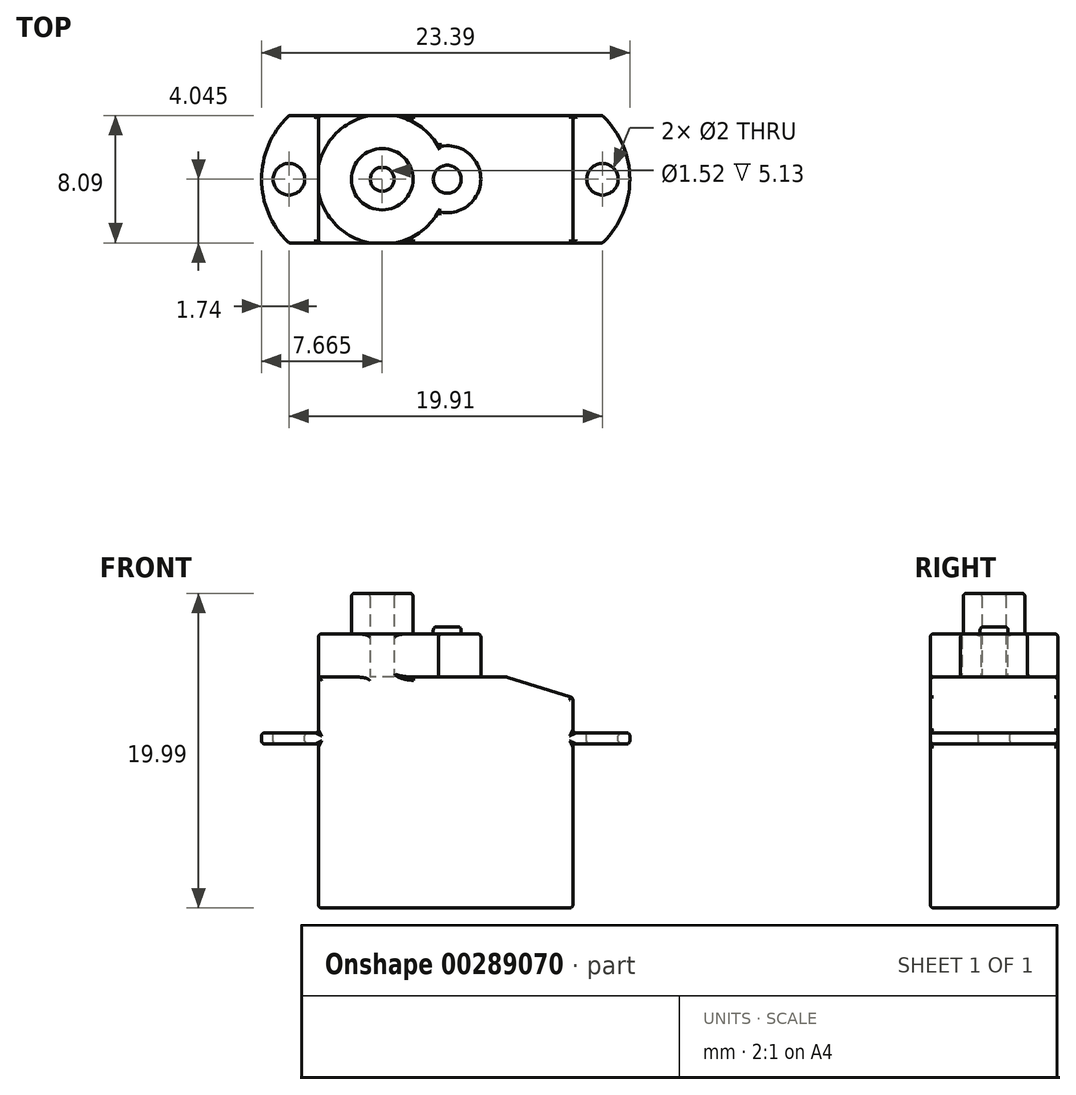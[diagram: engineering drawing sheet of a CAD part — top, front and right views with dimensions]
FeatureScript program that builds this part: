
annotation { "Feature Type Name" : "Feature", "Feature Type Description" : "" }
export const myFeature = defineFeature(function(context is Context, id is Id, definition is map)
    precondition{}
    {
        {
            var Q0;
            Q0=qCreatedBy(makeId("Top.planeOp"),FACE);
            var sketch = newSketch(context, id + "F0", { "sketchPlane" : qUnion([Q0])});
            skLineSegment(sketch, "E0.bottom", {"start": v(0, 0) * mm, "end": v(16.15, 0) * mm});
            skLineSegment(sketch, "E0.top", {"start": v(0, -8.1) * mm, "end": v(16.15, -8.1) * mm});
            skLineSegment(sketch, "E0.left", {"start": v(0, 0) * mm, "end": v(0, -8.1) * mm});
            skLineSegment(sketch, "E0.right", {"start": v(16.15, 0) * mm, "end": v(16.15, -8.1) * mm});
            skLineSegment(sketch, "E1", {"start": v(0, -4.05) * mm, "end": v(4.05, -4.05) * mm});
            skCircle(sketch, "E2", {"center": v(4.05, -4.05) * mm, "radius": 4.13 * mm});
            skCircle(sketch, "E3", {"center": v(8.18, -4.05) * mm, "radius": 2.13 * mm});
            skCircle(sketch, "E4", {"center": v(4.05, -4.05) * mm, "radius": 1.95 * mm});
            skCircle(sketch, "E5", {"center": v(8.18, -4.05) * mm, "radius": 0.9 * mm});
            skLineSegment(sketch, "E6", {"start": v(0, 0) * mm, "end": v(-1.88, 0) * mm});
            skLineSegment(sketch, "E7", {"start": v(-1.88, 0) * mm, "end": v(-1.88, -8.1) * mm});
            skLineSegment(sketch, "E8", {"start": v(-1.88, -8.1) * mm, "end": v(0, -8.1) * mm});
            skLineSegment(sketch, "E9", {"start": v(16.15, -8.1) * mm, "end": v(18.03, -8.1) * mm});
            skLineSegment(sketch, "E10", {"start": v(18.03, -8.1) * mm, "end": v(18.03, 0) * mm});
            skLineSegment(sketch, "E11", {"start": v(18.03, 0) * mm, "end": v(16.15, 0) * mm});
            skLineSegment(sketch, "E12", {"start": v(-1.88, -4.04) * mm, "end": v(-3.62, -4.04) * mm});
            skLineSegment(sketch, "E13", {"start": v(18.03, -4.04) * mm, "end": v(19.77, -4.04) * mm});
            skArc(sketch, "E14", {"start": v(-1.88, 0) * mm, "mid": v(-3.62, -4.04) * mm, "end": v(-1.88, -8.1) * mm});
            skArc(sketch, "E15", {"start": v(18.03, -8.1) * mm, "mid": v(19.77, -4.04) * mm, "end": v(18.03, 0) * mm});
            skCircle(sketch, "E16", {"center": v(4.05, -4.05) * mm, "radius": 0.76 * mm});
            skCircle(sketch, "E17", {"center": v(-1.88, -4.04) * mm, "radius": 1 * mm});
            skCircle(sketch, "E18", {"center": v(18.03, -4.04) * mm, "radius": 1 * mm});
            skSolve(sketch);
        }
        {
            var Q0;
            {var subQ0=sQuery(id+"F0.wireOp",EDGE,"E0.left");var subQ1=sQuery(id+"F0.wireOp",EDGE,"E0.bottom");var subQ2=makeQuery(id+"F0.imprint","INTERSECT",VERTEX,{"derivedFrom":[subQ1,subQ0]});Q0=makeQuery(id+"F0.imprint","IMPRINT",FACE,{"disambiguationData":[TD([[makeQuery(id+"F0.imprint","IMPRINT",EDGE,{"disambiguationData":[TD([[subQ2,-1.0]])],"derivedFrom":subQ1}),-1.0]])]});}
            var Q1;
            {var subQ0=sQuery(id+"F0.wireOp",EDGE,"E0.left");var subQ1=makeQuery(id+"F0.imprint","IMPRINT",VERTEX,{"derivedFrom":subQ0});Q1=makeQuery(id+"F0.imprint","IMPRINT",FACE,{"disambiguationData":[TD([[makeQuery(id+"F0.imprint","IMPRINT",EDGE,{"disambiguationData":[TD([[subQ1,1.0]])],"derivedFrom":subQ0}),1.0]])]});}
            var Q2;
            {var subQ0=sQuery(id+"F0.wireOp",EDGE,"E0.left");var subQ1=sQuery(id+"F0.wireOp",EDGE,"E0.top");var subQ2=makeQuery(id+"F0.imprint","INTERSECT",VERTEX,{"derivedFrom":[subQ1,subQ0]});Q2=makeQuery(id+"F0.imprint","IMPRINT",FACE,{"disambiguationData":[TD([[makeQuery(id+"F0.imprint","IMPRINT",EDGE,{"disambiguationData":[TD([[subQ2,-1.0]])],"derivedFrom":subQ1}),1.0]])]});}
            var Q3;
            {var subQ5=sQuery(id+"F0.wireOp",EDGE,"E0.right");Q3=makeQuery(id+"F0.imprint","IMPRINT",FACE,{"disambiguationData":[TD([[makeQuery(id+"F0.imprint","IMPRINT",EDGE,{"derivedFrom":subQ5}),-1.0]])]});}
            var Q4;
            {var subQ0=sQuery(id+"F0.wireOp",EDGE,"E3");var subQ1=sQuery(id+"F0.wireOp",EDGE,"E2");var subQ2=makeQuery(id+"F0.imprint","INTERSECT",VERTEX,{"disambiguationData":[OD(0.0)],"derivedFrom":[subQ1,subQ0]});Q4=makeQuery(id+"F0.imprint","IMPRINT",FACE,{"disambiguationData":[TD([[makeQuery(id+"F0.imprint","IMPRINT",EDGE,{"disambiguationData":[TD([[subQ2,1.0]])],"derivedFrom":subQ1}),-1.0]])]});}
            var Q5;
            {var subQ0=sQuery(id+"F0.wireOp",EDGE,"E3");var subQ1=sQuery(id+"F0.wireOp",EDGE,"E2");var subQ2=makeQuery(id+"F0.imprint","INTERSECT",VERTEX,{"disambiguationData":[OD(0.0)],"derivedFrom":[subQ1,subQ0]});Q5=makeQuery(id+"F0.imprint","IMPRINT",FACE,{"disambiguationData":[TD([[makeQuery(id+"F0.imprint","IMPRINT",EDGE,{"disambiguationData":[TD([[subQ2,1.0]])],"derivedFrom":subQ1}),1.0]])]});}
            var Q6;
            Q6=makeQuery(id+"F0.imprint","IMPRINT",FACE,{"disambiguationData":[TD([[makeQuery(id+"F0.imprint","IMPRINT",EDGE,{"derivedFrom":sQuery(id+"F0.wireOp",EDGE,"E4")}),1.0]])]});
            var Q7;
            {var subQ0=sQuery(id+"F0.wireOp",EDGE,"E5");var subQ1=sQuery(id+"F0.wireOp",EDGE,"E2");var subQ2=makeQuery(id+"F0.imprint","INTERSECT",VERTEX,{"disambiguationData":[OD(0.0)],"derivedFrom":[subQ1,subQ0]});Q7=makeQuery(id+"F0.imprint","IMPRINT",FACE,{"disambiguationData":[TD([[makeQuery(id+"F0.imprint","IMPRINT",EDGE,{"disambiguationData":[TD([[subQ2,1.0]])],"derivedFrom":subQ1}),-1.0]])]});}
            var Q8;
            {var subQ0=sQuery(id+"F0.wireOp",EDGE,"E5");var subQ1=sQuery(id+"F0.wireOp",EDGE,"E2");var subQ2=makeQuery(id+"F0.imprint","INTERSECT",VERTEX,{"disambiguationData":[OD(0.0)],"derivedFrom":[subQ1,subQ0]});Q8=makeQuery(id+"F0.imprint","IMPRINT",FACE,{"disambiguationData":[TD([[makeQuery(id+"F0.imprint","IMPRINT",EDGE,{"disambiguationData":[TD([[subQ2,1.0]])],"derivedFrom":subQ1}),1.0]])]});}
            var Q9;
            Q9=makeQuery(id+"F0.imprint","IMPRINT",FACE,{"disambiguationData":[TD([[makeQuery(id+"F0.imprint","IMPRINT",EDGE,{"derivedFrom":sQuery(id+"F0.wireOp",EDGE,"E16")}),1.0]])]});
            extrude(context, id + "F1", {"entities" : qUnion([Q0, Q1, Q2, Q3, Q4, Q5, Q6, Q7, Q8, Q9]), "oppositeDirection" : true, "depth" : 14.66 * mm});
        }
        {
            var Q0;
            Q0=makeQuery(id+"F0.imprint","IMPRINT",FACE,{"disambiguationData":[TD([[makeQuery(id+"F0.imprint","IMPRINT",EDGE,{"derivedFrom":sQuery(id+"F0.wireOp",EDGE,"E4")}),-1.0]])]});
            var Q1;
            {var subQ0=sQuery(id+"F0.wireOp",EDGE,"E3");var subQ1=sQuery(id+"F0.wireOp",EDGE,"E2");var subQ2=makeQuery(id+"F0.imprint","INTERSECT",VERTEX,{"disambiguationData":[OD(0.0)],"derivedFrom":[subQ1,subQ0]});Q1=makeQuery(id+"F0.imprint","IMPRINT",FACE,{"disambiguationData":[TD([[makeQuery(id+"F0.imprint","IMPRINT",EDGE,{"disambiguationData":[TD([[subQ2,1.0]])],"derivedFrom":subQ1}),1.0]])]});}
            var Q2;
            {var subQ0=sQuery(id+"F0.wireOp",EDGE,"E3");var subQ1=sQuery(id+"F0.wireOp",EDGE,"E2");var subQ2=makeQuery(id+"F0.imprint","INTERSECT",VERTEX,{"disambiguationData":[OD(0.0)],"derivedFrom":[subQ1,subQ0]});Q2=makeQuery(id+"F0.imprint","IMPRINT",FACE,{"disambiguationData":[TD([[makeQuery(id+"F0.imprint","IMPRINT",EDGE,{"disambiguationData":[TD([[subQ2,1.0]])],"derivedFrom":subQ1}),-1.0]])]});}
            extrude(context, id + "F2", {"entities" : qUnion([Q0, Q1, Q2]), "operationType" : NewBodyOperationType.ADD, "depth" : 2.75 * mm});
        }
        {
            var Q0;
            Q0=makeQuery(id+"F0.imprint","IMPRINT",FACE,{"disambiguationData":[TD([[makeQuery(id+"F0.imprint","IMPRINT",EDGE,{"derivedFrom":sQuery(id+"F0.wireOp",EDGE,"E4")}),1.0]])]});
            extrude(context, id + "F3", {"entities" : qUnion([Q0]), "operationType" : NewBodyOperationType.ADD, "depth" : 5.33 * mm});
        }
        {
            var Q0;
            Q0=makeQuery(id+"F2.boolean.opBoolean","SPLIT",FACE,{"disambiguationData":[TD([makeQuery(id+"F2.opExtrude","SWEPT_FACE",FACE,{"disambiguationData":[OSD([sQuery(id+"F0.wireOp",EDGE,"E5")])]})])],"derivedFrom":makeQuery(id+"F1.opExtrude","CAP_FACE",FACE,{"disambiguationData":[OSD([sQuery(id+"F0.wireOp",EDGE,"E0.bottom"),sQuery(id+"F0.wireOp",EDGE,"E0.top"),sQuery(id+"F0.wireOp",EDGE,"E0.left"),sQuery(id+"F0.wireOp",EDGE,"E0.right")])],"isStart":true})});
            extrude(context, id + "F4", {"entities" : qUnion([Q0]), "operationType" : NewBodyOperationType.ADD, "depth" : 3.19 * mm});
        }
        {
            var Q0;
            {var subQ4=sQuery(id+"F0.wireOp",EDGE,"E6");Q0=makeQuery(id+"F0.imprint","IMPRINT",FACE,{"disambiguationData":[TD([[makeQuery(id+"F0.imprint","IMPRINT",EDGE,{"derivedFrom":subQ4}),1.0]])]});}
            var Q1;
            Q1=makeQuery(id+"F0.imprint","IMPRINT",FACE,{"disambiguationData":[TD([[makeQuery(id+"F0.imprint","IMPRINT",EDGE,{"derivedFrom":sQuery(id+"F0.wireOp",EDGE,"E0.right")}),1.0]])]});
            var Q2;
            {var subQ0=sQuery(id+"F0.wireOp",EDGE,"E14");var subQ5=sQuery(id+"F0.wireOp",EDGE,"E12");var subQ6=makeQuery(id+"F0.imprint","INTERSECT",VERTEX,{"derivedFrom":[subQ5,subQ0]});Q2=makeQuery(id+"F0.imprint","IMPRINT",FACE,{"disambiguationData":[TD([[makeQuery(id+"F0.imprint","IMPRINT",EDGE,{"disambiguationData":[TD([[subQ6,1.0]])],"derivedFrom":subQ5}),1.0]])]});}
            var Q3;
            {var subQ0=sQuery(id+"F0.wireOp",EDGE,"E14");var subQ5=sQuery(id+"F0.wireOp",EDGE,"E12");var subQ6=makeQuery(id+"F0.imprint","INTERSECT",VERTEX,{"derivedFrom":[subQ5,subQ0]});Q3=makeQuery(id+"F0.imprint","IMPRINT",FACE,{"disambiguationData":[TD([[makeQuery(id+"F0.imprint","IMPRINT",EDGE,{"disambiguationData":[TD([[subQ6,1.0]])],"derivedFrom":subQ5}),-1.0]])]});}
            var Q4;
            {var subQ0=sQuery(id+"F0.wireOp",EDGE,"E15");var subQ5=sQuery(id+"F0.wireOp",EDGE,"E13");var subQ6=makeQuery(id+"F0.imprint","INTERSECT",VERTEX,{"derivedFrom":[subQ5,subQ0]});Q4=makeQuery(id+"F0.imprint","IMPRINT",FACE,{"disambiguationData":[TD([[makeQuery(id+"F0.imprint","IMPRINT",EDGE,{"disambiguationData":[TD([[subQ6,1.0]])],"derivedFrom":subQ5}),-1.0]])]});}
            var Q5;
            {var subQ0=sQuery(id+"F0.wireOp",EDGE,"E15");var subQ5=sQuery(id+"F0.wireOp",EDGE,"E13");var subQ6=makeQuery(id+"F0.imprint","INTERSECT",VERTEX,{"derivedFrom":[subQ5,subQ0]});Q5=makeQuery(id+"F0.imprint","IMPRINT",FACE,{"disambiguationData":[TD([[makeQuery(id+"F0.imprint","IMPRINT",EDGE,{"disambiguationData":[TD([[subQ6,1.0]])],"derivedFrom":subQ5}),1.0]])]});}
            var Q6;
            {var subQ0=sQuery(id+"F0.wireOp",EDGE,"E0.left");var subQ1=makeQuery(id+"F0.imprint","IMPRINT",VERTEX,{"derivedFrom":subQ0});Q6=makeQuery(id+"F0.imprint","IMPRINT",FACE,{"disambiguationData":[TD([[makeQuery(id+"F0.imprint","IMPRINT",EDGE,{"disambiguationData":[TD([[subQ1,1.0]])],"derivedFrom":subQ0}),-1.0]])]});}
            extrude(context, id + "F5", {"entities" : qUnion([Q0, Q1, Q2, Q3, Q4, Q5, Q6]), "operationType" : NewBodyOperationType.ADD, "oppositeDirection" : true, "depth" : 4.24 * mm, "hasSecondDirection" : true, "secondDirectionOppositeDirection" : true, "secondDirectionDepth" : 3.54 * mm});
        }
        {
            var Q0;
            {var subQ0=sQuery(id+"F0.wireOp",EDGE,"E0.top");Q0=makeQuery(id+"F5.boolean.opBoolean","MERGE",FACE,{"derivedFrom":[makeQuery(id+"F2.boolean.opBoolean","MERGE",FACE,{"derivedFrom":[makeQuery(id+"F1.opExtrude","SWEPT_FACE",FACE,{"disambiguationData":[OSD([subQ0])]}),makeQuery(id+"F2.opExtrude","SWEPT_FACE",FACE,{"disambiguationData":[OSD([subQ0])]})]}),makeQuery(id+"F5.opExtrude","SWEPT_FACE",FACE,{"disambiguationData":[OSD([sQuery(id+"F0.wireOp",EDGE,"E8")])]}),makeQuery(id+"F5.opExtrude","SWEPT_FACE",FACE,{"disambiguationData":[OSD([sQuery(id+"F0.wireOp",EDGE,"E9")])]})]});}
            var sketch = newSketch(context, id + "F6", { "sketchPlane" : qUnion([Q0])});
            skLineSegment(sketch, "E19", {"start": v(16.15, 0) * mm, "end": v(11.96, 0) * mm});
            skLineSegment(sketch, "E20", {"start": v(16.15, 0) * mm, "end": v(16.15, -1.3) * mm});
            skLineSegment(sketch, "E21", {"start": v(16.15, -1.3) * mm, "end": v(11.96, 0) * mm});
            skSolve(sketch);
        }
        {
            var Q0;
            Q0=makeQuery(id+"F6.imprint","IMPRINT",FACE,{"disambiguationData":[TD([[makeQuery(id+"F6.imprint","IMPRINT",EDGE,{"derivedFrom":sQuery(id+"F6.wireOp",EDGE,"E19")}),-1.0]])]});
            extrude(context, id + "F7", {"entities" : qUnion([Q0]), "operationType" : NewBodyOperationType.REMOVE, "oppositeDirection" : true, "depth" : 25 * mm});
        }
        {
            var Q0;
            {var subQ0=sQuery(id+"F0.wireOp",EDGE,"E0.top");Q0=makeQuery(id+"F5.boolean.opBoolean","MERGE",FACE,{"derivedFrom":[makeQuery(id+"F2.boolean.opBoolean","MERGE",FACE,{"derivedFrom":[makeQuery(id+"F1.opExtrude","SWEPT_FACE",FACE,{"disambiguationData":[OSD([subQ0])]}),makeQuery(id+"F2.opExtrude","SWEPT_FACE",FACE,{"disambiguationData":[OSD([subQ0])]})]}),makeQuery(id+"F5.opExtrude","SWEPT_FACE",FACE,{"disambiguationData":[OSD([sQuery(id+"F0.wireOp",EDGE,"E8")])]}),makeQuery(id+"F5.opExtrude","SWEPT_FACE",FACE,{"disambiguationData":[OSD([sQuery(id+"F0.wireOp",EDGE,"E9")])]})]});}
            var Q1;
            {var subQ0=sQuery(id+"F0.wireOp",EDGE,"E0.bottom");Q1=makeQuery(id+"F5.boolean.opBoolean","MERGE",FACE,{"derivedFrom":[makeQuery(id+"F2.boolean.opBoolean","MERGE",FACE,{"derivedFrom":[makeQuery(id+"F1.opExtrude","SWEPT_FACE",FACE,{"disambiguationData":[OSD([subQ0])]}),makeQuery(id+"F2.opExtrude","SWEPT_FACE",FACE,{"disambiguationData":[OSD([subQ0])]})]}),makeQuery(id+"F5.opExtrude","SWEPT_FACE",FACE,{"disambiguationData":[OSD([sQuery(id+"F0.wireOp",EDGE,"E6")])]}),makeQuery(id+"F5.opExtrude","SWEPT_FACE",FACE,{"disambiguationData":[OSD([sQuery(id+"F0.wireOp",EDGE,"E11")])]})]});}
            var Q2;
            Q2=makeQuery(id+"F3.opExtrude","CAP_FACE",FACE,{"disambiguationData":[OSD([sQuery(id+"F0.wireOp",EDGE,"E4"),sQuery(id+"F0.wireOp",EDGE,"E16")])],"isStart":false});
            var Q3;
            Q3=makeQuery(id+"F4.opExtrude","CAP_FACE",FACE,{"disambiguationData":[OSD([sQuery(id+"F0.wireOp",EDGE,"E0.bottom"),sQuery(id+"F0.wireOp",EDGE,"E0.top"),sQuery(id+"F0.wireOp",EDGE,"E0.left"),sQuery(id+"F0.wireOp",EDGE,"E0.right")])],"isStart":false});
            var Q4;
            {var subQ0=sQuery(id+"F0.wireOp",EDGE,"E0.bottom");var subQ1=sQuery(id+"F0.wireOp",EDGE,"E0.top");var subQ2=sQuery(id+"F0.wireOp",EDGE,"E0.right");Q4=makeQuery(id+"F2.boolean.opBoolean","SPLIT",FACE,{"disambiguationData":[TD([makeQuery(id+"F1.opExtrude","SWEPT_FACE",FACE,{"disambiguationData":[OSD([subQ2])]})])],"derivedFrom":makeQuery(id+"F1.opExtrude","CAP_FACE",FACE,{"disambiguationData":[OSD([subQ0,subQ1,sQuery(id+"F0.wireOp",EDGE,"E0.left"),subQ2])],"isStart":true})});}
            var Q5;
            {var subQ0=sQuery(id+"F0.wireOp",EDGE,"E0.left");var subQ1=sQuery(id+"F0.wireOp",EDGE,"E0.top");var subQ2=sQuery(id+"F0.wireOp",EDGE,"E2");Q5=makeQuery(id+"F2.boolean.opBoolean","SPLIT",FACE,{"disambiguationData":[TD([makeQuery(id+"F2.opExtrude","SWEPT_FACE",FACE,{"disambiguationData":[OSD([subQ2]),TDD([makeQuery(id+"F0.imprint","IMPRINT",EDGE,{"disambiguationData":[TD([[makeQuery(id+"F0.imprint","INTERSECT",VERTEX,{"disambiguationData":[OD(0.0)],"derivedFrom":[subQ1,subQ2]}),1.0]])],"derivedFrom":subQ2})])]})])],"derivedFrom":makeQuery(id+"F1.opExtrude","CAP_FACE",FACE,{"disambiguationData":[OSD([sQuery(id+"F0.wireOp",EDGE,"E0.bottom"),subQ1,subQ0,sQuery(id+"F0.wireOp",EDGE,"E0.right")])],"isStart":true})});}
            var Q6;
            {var subQ0=sQuery(id+"F0.wireOp",EDGE,"E0.bottom");var subQ1=sQuery(id+"F0.wireOp",EDGE,"E0.left");var subQ2=sQuery(id+"F0.wireOp",EDGE,"E2");Q6=makeQuery(id+"F2.boolean.opBoolean","SPLIT",FACE,{"disambiguationData":[TD([makeQuery(id+"F2.opExtrude","SWEPT_FACE",FACE,{"disambiguationData":[OSD([subQ2]),TDD([makeQuery(id+"F0.imprint","IMPRINT",EDGE,{"disambiguationData":[TD([[makeQuery(id+"F0.imprint","INTERSECT",VERTEX,{"disambiguationData":[OD(0.0)],"derivedFrom":[subQ0,subQ2]}),-1.0]])],"derivedFrom":subQ2})])]})])],"derivedFrom":makeQuery(id+"F1.opExtrude","CAP_FACE",FACE,{"disambiguationData":[OSD([subQ0,sQuery(id+"F0.wireOp",EDGE,"E0.top"),subQ1,sQuery(id+"F0.wireOp",EDGE,"E0.right")])],"isStart":true})});}
            var Q7;
            {var subQ0=sQuery(id+"F0.wireOp",EDGE,"E2");Q7=makeQuery(id+"F2.opExtrude","CAP_EDGE",EDGE,{"disambiguationData":[OSD([subQ0]),TDD([makeQuery(id+"F0.imprint","IMPRINT",EDGE,{"disambiguationData":[TD([[makeQuery(id+"F0.imprint","INTERSECT",VERTEX,{"disambiguationData":[OD(1.0)],"derivedFrom":[sQuery(id+"F0.wireOp",EDGE,"E0.top"),subQ0]}),-1.0]])],"derivedFrom":subQ0})])],"isStart":false});}
            var Q8;
            {var subQ0=sQuery(id+"F0.wireOp",EDGE,"E2");Q8=makeQuery(id+"F2.opExtrude","CAP_EDGE",EDGE,{"disambiguationData":[OSD([subQ0]),TDD([makeQuery(id+"F0.imprint","IMPRINT",EDGE,{"disambiguationData":[TD([[makeQuery(id+"F0.imprint","INTERSECT",VERTEX,{"disambiguationData":[OD(0.0)],"derivedFrom":[sQuery(id+"F0.wireOp",EDGE,"E0.top"),subQ0]}),1.0]])],"derivedFrom":subQ0})])],"isStart":false});}
            var Q9;
            Q9=makeQuery(id+"F2.opExtrude","CAP_EDGE",EDGE,{"disambiguationData":[OSD([sQuery(id+"F0.wireOp",EDGE,"E3")])],"isStart":false});
            var Q10;
            {var subQ0=sQuery(id+"F0.wireOp",EDGE,"E2");Q10=makeQuery(id+"F2.opExtrude","CAP_EDGE",EDGE,{"disambiguationData":[OSD([subQ0]),TDD([makeQuery(id+"F0.imprint","IMPRINT",EDGE,{"disambiguationData":[TD([[makeQuery(id+"F0.imprint","INTERSECT",VERTEX,{"disambiguationData":[OD(1.0)],"derivedFrom":[sQuery(id+"F0.wireOp",EDGE,"E0.bottom"),subQ0]}),1.0]])],"derivedFrom":subQ0})])],"isStart":false});}
            var Q11;
            {var subQ0=sQuery(id+"F0.wireOp",EDGE,"E2");Q11=makeQuery(id+"F2.opExtrude","CAP_EDGE",EDGE,{"disambiguationData":[OSD([subQ0]),TDD([makeQuery(id+"F0.imprint","IMPRINT",EDGE,{"disambiguationData":[TD([[makeQuery(id+"F0.imprint","INTERSECT",VERTEX,{"disambiguationData":[OD(0.0)],"derivedFrom":[sQuery(id+"F0.wireOp",EDGE,"E0.bottom"),subQ0]}),-1.0]])],"derivedFrom":subQ0})])],"isStart":false});}
            var Q12;
            Q12=makeQuery(id+"F2.opExtrude","CAP_EDGE",EDGE,{"disambiguationData":[OSD([sQuery(id+"F0.wireOp",EDGE,"E0.left")])],"isStart":false});
            fillet(context, id + "F8", {"entities" : qUnion([Q0, Q1, Q2, Q3, Q4, Q5, Q6, Q7, Q8, Q9, Q10, Q11, Q12]), "radius" : 0.2 * mm, "tangentPropagation" : true, "allowEdgeOverflow" : false});
        }
        {
            var Q0;
            Q0=makeQuery(id+"F7.boolean.opBoolean","COPY",FACE,{"derivedFrom":makeQuery(id+"F7.opExtrude","SWEPT_FACE",FACE,{"disambiguationData":[OSD([sQuery(id+"F6.wireOp",EDGE,"E21")])]})});
            var Q1;
            Q1=makeQuery(id+"F5.opExtrude","CAP_FACE",FACE,{"disambiguationData":[OSD([sQuery(id+"F0.wireOp",EDGE,"E0.right"),sQuery(id+"F0.wireOp",EDGE,"E9"),sQuery(id+"F0.wireOp",EDGE,"E11"),sQuery(id+"F0.wireOp",EDGE,"E15"),sQuery(id+"F0.wireOp",EDGE,"E18")])],"isStart":true});
            var Q2;
            Q2=makeQuery(id+"F5.opExtrude","CAP_FACE",FACE,{"disambiguationData":[OSD([sQuery(id+"F0.wireOp",EDGE,"E0.right"),sQuery(id+"F0.wireOp",EDGE,"E9"),sQuery(id+"F0.wireOp",EDGE,"E11"),sQuery(id+"F0.wireOp",EDGE,"E15"),sQuery(id+"F0.wireOp",EDGE,"E18")])],"isStart":false});
            var Q3;
            Q3=makeQuery(id+"F5.opExtrude","CAP_FACE",FACE,{"disambiguationData":[OSD([sQuery(id+"F0.wireOp",EDGE,"E0.left"),sQuery(id+"F0.wireOp",EDGE,"E6"),sQuery(id+"F0.wireOp",EDGE,"E8"),sQuery(id+"F0.wireOp",EDGE,"E14"),sQuery(id+"F0.wireOp",EDGE,"E17")])],"isStart":false});
            var Q4;
            Q4=makeQuery(id+"F5.opExtrude","CAP_FACE",FACE,{"disambiguationData":[OSD([sQuery(id+"F0.wireOp",EDGE,"E0.left"),sQuery(id+"F0.wireOp",EDGE,"E6"),sQuery(id+"F0.wireOp",EDGE,"E8"),sQuery(id+"F0.wireOp",EDGE,"E14"),sQuery(id+"F0.wireOp",EDGE,"E17")])],"isStart":true});
            var Q5;
            Q5=makeQuery(id+"F1.opExtrude","CAP_FACE",FACE,{"disambiguationData":[OSD([sQuery(id+"F0.wireOp",EDGE,"E0.bottom"),sQuery(id+"F0.wireOp",EDGE,"E0.top"),sQuery(id+"F0.wireOp",EDGE,"E0.left"),sQuery(id+"F0.wireOp",EDGE,"E0.right")])],"isStart":false});
            fillet(context, id + "F9", {"entities" : qUnion([Q0, Q1, Q2, Q3, Q4, Q5]), "radius" : 0.2 * mm, "tangentPropagation" : true, "allowEdgeOverflow" : false});
        }
    });
